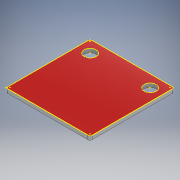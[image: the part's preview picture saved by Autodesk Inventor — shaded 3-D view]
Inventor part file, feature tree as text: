
AUTODESK INVENTOR PART (.ipt)
format: ipt  version: 2017 (Build 210142000, 142)  size: 126,464 bytes
history: native  units: mm
features: sketch x2, extrude x1, projected_geometry x1
ambient origin geometry x8: Origin, YZ Plane, XZ Plane, XY Plane, X Axis, Y Axis, Z Axis, Center Point
bodies: Solid1 (feature_tree)
feature tree (4):
  extrude  "Extrusion1"  Depth=1.5mm
  sketch  "Sketch2"  dims[d6=1.5mm d7=3.0mm d8=1.5mm d9=1.5mm d10=1.0mm d11=0.0mm]
  sketch  "Sketch1"  dims[d4=1.5mm d5=3.0mm]
  projected_geometry  "Projected Loop1"
